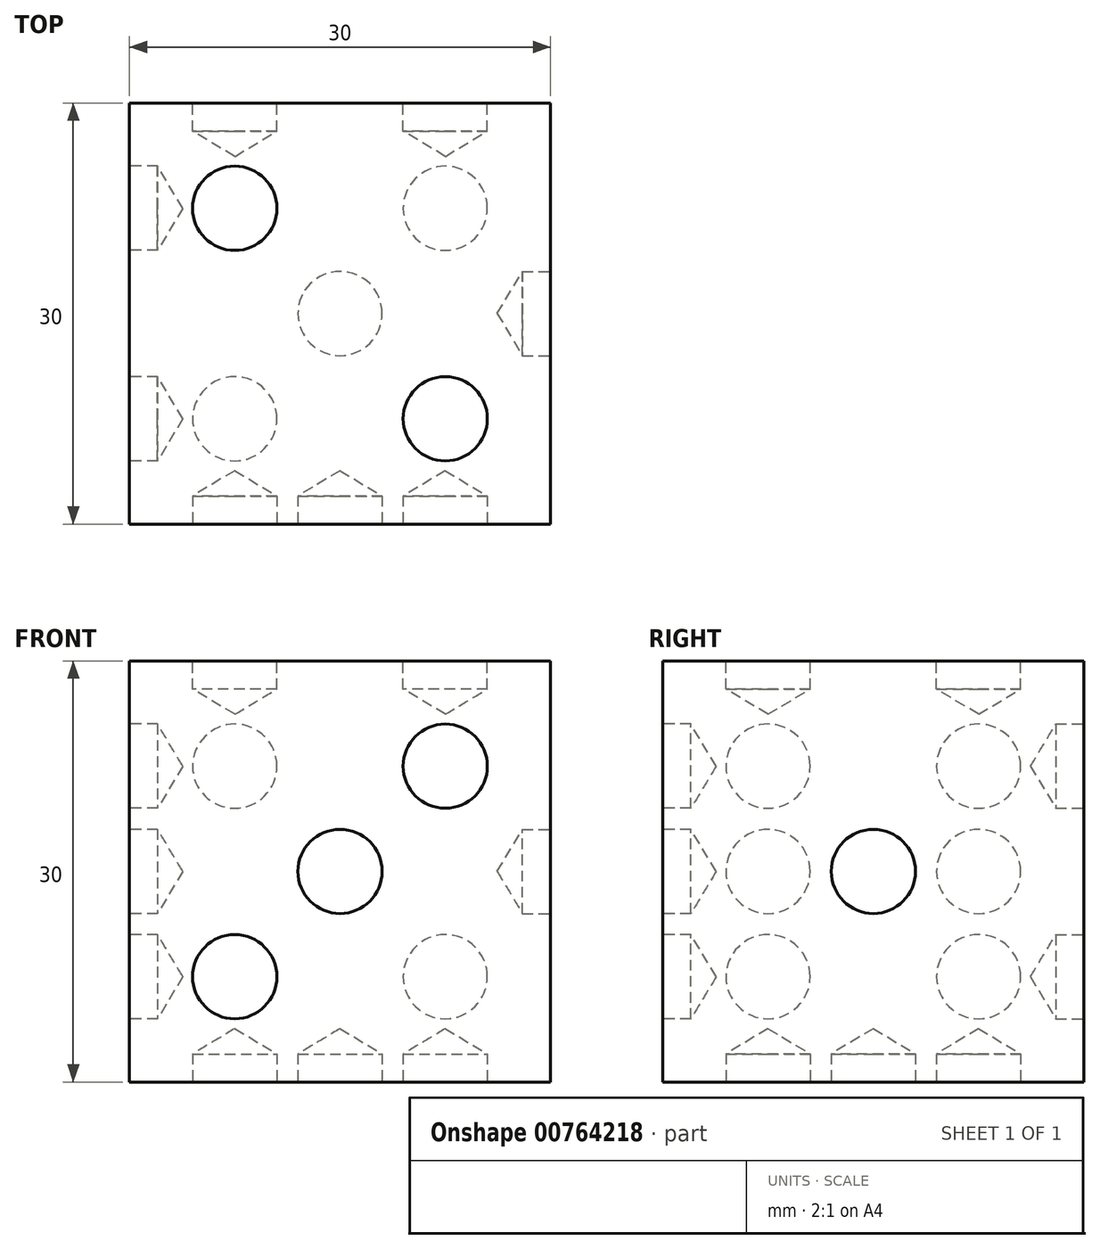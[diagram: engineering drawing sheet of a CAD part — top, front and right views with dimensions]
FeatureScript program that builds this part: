
annotation { "Feature Type Name" : "Feature", "Feature Type Description" : "" }
export const myFeature = defineFeature(function(context is Context, id is Id, definition is map)
    precondition{}
    {
        {
            var Q0;
            Q0=qCreatedBy(makeId("Front.planeOp"),FACE);
            var sketch = newSketch(context, id + "F0", { "sketchPlane" : qUnion([Q0])});
            skLineSegment(sketch, "E0.bottom", {"start": v(-15, 15) * mm, "end": v(15, 15) * mm});
            skLineSegment(sketch, "E0.top", {"start": v(-15, -15) * mm, "end": v(15, -15) * mm});
            skLineSegment(sketch, "E0.left", {"start": v(-15, 15) * mm, "end": v(-15, -15) * mm});
            skLineSegment(sketch, "E0.right", {"start": v(15, 15) * mm, "end": v(15, -15) * mm});
            skPoint(sketch, "E0.middle", {"position": v(0, 0) * mm});
            skSolve(sketch);
        }
        {
            var Q0;
            Q0=makeQuery(id+"F0.imprint","IMPRINT",FACE,{"disambiguationData":[TD([[makeQuery(id+"F0.imprint","IMPRINT",EDGE,{"derivedFrom":sQuery(id+"F0.wireOp",EDGE,"E0.bottom")}),-1.0]])]});
            extrude(context, id + "F1", {"entities" : qUnion([Q0]), "endBound" : BoundingType.SYMMETRIC, "depth" : 30 * mm, "offsetDistance" : 25 * mm});
        }
        {
            var Q0;
            Q0=makeQuery(id+"F1.opExtrude","CAP_FACE",FACE,{"disambiguationData":[OSD([sQuery(id+"F0.wireOp",EDGE,"E0.bottom"),sQuery(id+"F0.wireOp",EDGE,"E0.top"),sQuery(id+"F0.wireOp",EDGE,"E0.left"),sQuery(id+"F0.wireOp",EDGE,"E0.right")])],"isStart":false});
            var sketch = newSketch(context, id + "F2", { "sketchPlane" : qUnion([Q0])});
            skLineSegment(sketch, "E1", {"start": v(0, 15) * mm, "end": v(15, 0) * mm});
            skLineSegment(sketch, "E2", {"start": v(15, 0) * mm, "end": v(0, -15) * mm});
            skLineSegment(sketch, "E3", {"start": v(0, -15) * mm, "end": v(-15, 0) * mm});
            skLineSegment(sketch, "E4", {"start": v(-15, 0) * mm, "end": v(0, 15) * mm});
            skLineSegment(sketch, "E5", {"start": v(-15, 15) * mm, "end": v(15, -15) * mm});
            skLineSegment(sketch, "E6", {"start": v(15, 15) * mm, "end": v(-15, -15) * mm});
            skLineSegment(sketch, "E7", {"start": v(-7.5, -7.5) * mm, "end": v(7.5, -7.5) * mm});
            skLineSegment(sketch, "E8", {"start": v(7.5, -7.5) * mm, "end": v(7.5, 7.5) * mm});
            skLineSegment(sketch, "E9", {"start": v(7.5, 7.5) * mm, "end": v(-7.5, 7.5) * mm});
            skLineSegment(sketch, "E10", {"start": v(-7.5, 7.5) * mm, "end": v(-7.5, -7.5) * mm});
            skLineSegment(sketch, "E11", {"start": v(-7.5, 0) * mm, "end": v(7.5, 0) * mm});
            skLineSegment(sketch, "E12", {"start": v(0, 7.5) * mm, "end": v(0, -7.5) * mm});
            skPoint(sketch, "E13", {"position": v(0, 0) * mm});
            skSolve(sketch);
        }
        {
            var Q0;
            Q0=makeQuery(id+"F1.opExtrude","SWEPT_FACE",FACE,{"disambiguationData":[OSD([sQuery(id+"F0.wireOp",EDGE,"E0.right")])]});
            var sketch = newSketch(context, id + "F3", { "sketchPlane" : qUnion([Q0])});
            skLineSegment(sketch, "E14", {"start": v(0, 15) * mm, "end": v(15, 0) * mm});
            skLineSegment(sketch, "E15", {"start": v(15, 0) * mm, "end": v(0, -15) * mm});
            skLineSegment(sketch, "E16", {"start": v(0, -15) * mm, "end": v(-15, 0) * mm});
            skLineSegment(sketch, "E17", {"start": v(-15, 0) * mm, "end": v(0, 15) * mm});
            skLineSegment(sketch, "E18", {"start": v(-15, 15) * mm, "end": v(15, -15) * mm});
            skLineSegment(sketch, "E19", {"start": v(15, 15) * mm, "end": v(-15, -15) * mm});
            skLineSegment(sketch, "E20", {"start": v(-7.5, -7.5) * mm, "end": v(7.5, -7.5) * mm});
            skLineSegment(sketch, "E21", {"start": v(7.5, -7.5) * mm, "end": v(7.5, 7.5) * mm});
            skLineSegment(sketch, "E22", {"start": v(7.5, 7.5) * mm, "end": v(-7.5, 7.5) * mm});
            skLineSegment(sketch, "E23", {"start": v(-7.5, 7.5) * mm, "end": v(-7.5, -7.5) * mm});
            skLineSegment(sketch, "E24", {"start": v(-7.5, 0) * mm, "end": v(7.5, 0) * mm});
            skLineSegment(sketch, "E25", {"start": v(0, 7.5) * mm, "end": v(0, -7.5) * mm});
            skPoint(sketch, "E26", {"position": v(0, 0) * mm});
            skSolve(sketch);
        }
        {
            var Q0;
            Q0=makeQuery(id+"F1.opExtrude","SWEPT_FACE",FACE,{"disambiguationData":[OSD([sQuery(id+"F0.wireOp",EDGE,"E0.bottom")])]});
            var sketch = newSketch(context, id + "F4", { "sketchPlane" : qUnion([Q0])});
            skLineSegment(sketch, "E27", {"start": v(0, 15) * mm, "end": v(15, 0) * mm});
            skLineSegment(sketch, "E28", {"start": v(15, 0) * mm, "end": v(0, -15) * mm});
            skLineSegment(sketch, "E29", {"start": v(0, -15) * mm, "end": v(-15, 0) * mm});
            skLineSegment(sketch, "E30", {"start": v(-15, 0) * mm, "end": v(0, 15) * mm});
            skLineSegment(sketch, "E31", {"start": v(-15, 15) * mm, "end": v(15, -15) * mm});
            skLineSegment(sketch, "E32", {"start": v(15, 15) * mm, "end": v(-15, -15) * mm});
            skLineSegment(sketch, "E33", {"start": v(-7.5, -7.5) * mm, "end": v(7.5, -7.5) * mm});
            skLineSegment(sketch, "E34", {"start": v(7.5, -7.5) * mm, "end": v(7.5, 7.5) * mm});
            skLineSegment(sketch, "E35", {"start": v(7.5, 7.5) * mm, "end": v(-7.5, 7.5) * mm});
            skLineSegment(sketch, "E36", {"start": v(-7.5, 7.5) * mm, "end": v(-7.5, -7.5) * mm});
            skLineSegment(sketch, "E37", {"start": v(-7.5, 0) * mm, "end": v(7.5, 0) * mm});
            skLineSegment(sketch, "E38", {"start": v(0, 7.5) * mm, "end": v(0, -7.5) * mm});
            skPoint(sketch, "E39", {"position": v(0, 0) * mm});
            skSolve(sketch);
        }
        {
            var Q0;
            Q0=makeQuery(id+"F1.opExtrude","CAP_FACE",FACE,{"disambiguationData":[OSD([sQuery(id+"F0.wireOp",EDGE,"E0.bottom"),sQuery(id+"F0.wireOp",EDGE,"E0.top"),sQuery(id+"F0.wireOp",EDGE,"E0.left"),sQuery(id+"F0.wireOp",EDGE,"E0.right")])],"isStart":true});
            var sketch = newSketch(context, id + "F5", { "sketchPlane" : qUnion([Q0])});
            skLineSegment(sketch, "E40", {"start": v(0, 15) * mm, "end": v(15, 0) * mm});
            skLineSegment(sketch, "E41", {"start": v(15, 0) * mm, "end": v(0, -15) * mm});
            skLineSegment(sketch, "E42", {"start": v(0, -15) * mm, "end": v(-15, 0) * mm});
            skLineSegment(sketch, "E43", {"start": v(-15, 0) * mm, "end": v(0, 15) * mm});
            skLineSegment(sketch, "E44", {"start": v(-15, 15) * mm, "end": v(15, -15) * mm});
            skLineSegment(sketch, "E45", {"start": v(15, 15) * mm, "end": v(-15, -15) * mm});
            skLineSegment(sketch, "E46", {"start": v(-7.5, -7.5) * mm, "end": v(7.5, -7.5) * mm});
            skLineSegment(sketch, "E47", {"start": v(7.5, -7.5) * mm, "end": v(7.5, 7.5) * mm});
            skLineSegment(sketch, "E48", {"start": v(7.5, 7.5) * mm, "end": v(-7.5, 7.5) * mm});
            skLineSegment(sketch, "E49", {"start": v(-7.5, 7.5) * mm, "end": v(-7.5, -7.5) * mm});
            skLineSegment(sketch, "E50", {"start": v(-7.5, 0) * mm, "end": v(7.5, 0) * mm});
            skLineSegment(sketch, "E51", {"start": v(0, 7.5) * mm, "end": v(0, -7.5) * mm});
            skPoint(sketch, "E52", {"position": v(0, 0) * mm});
            skSolve(sketch);
        }
        {
            var Q0;
            Q0=makeQuery(id+"F1.opExtrude","SWEPT_FACE",FACE,{"disambiguationData":[OSD([sQuery(id+"F0.wireOp",EDGE,"E0.top")])]});
            var sketch = newSketch(context, id + "F6", { "sketchPlane" : qUnion([Q0])});
            skLineSegment(sketch, "E53", {"start": v(0, 15) * mm, "end": v(15, 0) * mm});
            skLineSegment(sketch, "E54", {"start": v(15, 0) * mm, "end": v(0, -15) * mm});
            skLineSegment(sketch, "E55", {"start": v(0, -15) * mm, "end": v(-15, 0) * mm});
            skLineSegment(sketch, "E56", {"start": v(-15, 0) * mm, "end": v(0, 15) * mm});
            skLineSegment(sketch, "E57", {"start": v(-15, 15) * mm, "end": v(15, -15) * mm});
            skLineSegment(sketch, "E58", {"start": v(15, 15) * mm, "end": v(-15, -15) * mm});
            skLineSegment(sketch, "E59", {"start": v(-7.5, -7.5) * mm, "end": v(7.5, -7.5) * mm});
            skLineSegment(sketch, "E60", {"start": v(7.5, -7.5) * mm, "end": v(7.5, 7.5) * mm});
            skLineSegment(sketch, "E61", {"start": v(7.5, 7.5) * mm, "end": v(-7.5, 7.5) * mm});
            skLineSegment(sketch, "E62", {"start": v(-7.5, 7.5) * mm, "end": v(-7.5, -7.5) * mm});
            skLineSegment(sketch, "E63", {"start": v(-7.5, 0) * mm, "end": v(7.5, 0) * mm});
            skLineSegment(sketch, "E64", {"start": v(0, 7.5) * mm, "end": v(0, -7.5) * mm});
            skPoint(sketch, "E65", {"position": v(0, 0) * mm});
            skSolve(sketch);
        }
        {
            var Q0;
            Q0=makeQuery(id+"F1.opExtrude","SWEPT_FACE",FACE,{"disambiguationData":[OSD([sQuery(id+"F0.wireOp",EDGE,"E0.left")])]});
            var sketch = newSketch(context, id + "F7", { "sketchPlane" : qUnion([Q0])});
            skLineSegment(sketch, "E66", {"start": v(0, 15) * mm, "end": v(15, 0) * mm});
            skLineSegment(sketch, "E67", {"start": v(15, 0) * mm, "end": v(0, -15) * mm});
            skLineSegment(sketch, "E68", {"start": v(0, -15) * mm, "end": v(-15, 0) * mm});
            skLineSegment(sketch, "E69", {"start": v(-15, 0) * mm, "end": v(0, 15) * mm});
            skLineSegment(sketch, "E70", {"start": v(-15, 15) * mm, "end": v(15, -15) * mm});
            skLineSegment(sketch, "E71", {"start": v(15, 15) * mm, "end": v(-15, -15) * mm});
            skLineSegment(sketch, "E72", {"start": v(-7.5, -7.5) * mm, "end": v(7.5, -7.5) * mm});
            skLineSegment(sketch, "E73", {"start": v(7.5, -7.5) * mm, "end": v(7.5, 7.5) * mm});
            skLineSegment(sketch, "E74", {"start": v(7.5, 7.5) * mm, "end": v(-7.5, 7.5) * mm});
            skLineSegment(sketch, "E75", {"start": v(-7.5, 7.5) * mm, "end": v(-7.5, -7.5) * mm});
            skLineSegment(sketch, "E76", {"start": v(-7.5, 0) * mm, "end": v(7.5, 0) * mm});
            skLineSegment(sketch, "E77", {"start": v(0, 7.5) * mm, "end": v(0, -7.5) * mm});
            skPoint(sketch, "E78", {"position": v(0, 0) * mm});
            skSolve(sketch);
        }
        {
            var Q0;
            Q0=sQuery(id+"F2.wireOp",VERTEX,"E9.start");
            var Q1;
            Q1=sQuery(id+"F2.wireOp",VERTEX,"E13");
            var Q2;
            Q2=sQuery(id+"F2.wireOp",VERTEX,"E10.end");
            var Q3;
            Q3=sQuery(id+"F5.wireOp",VERTEX,"E49.start");
            var Q4;
            Q4=sQuery(id+"F5.wireOp",VERTEX,"E47.end");
            var Q5;
            Q5=sQuery(id+"F5.wireOp",VERTEX,"E47.start");
            var Q6;
            Q6=sQuery(id+"F5.wireOp",VERTEX,"E49.end");
            var Q7;
            Q7=sQuery(id+"F7.wireOp",VERTEX,"E75.start");
            var Q8;
            Q8=sQuery(id+"F7.wireOp",VERTEX,"E76.start");
            var Q9;
            Q9=sQuery(id+"F7.wireOp",VERTEX,"E75.end");
            var Q10;
            Q10=sQuery(id+"F7.wireOp",VERTEX,"E73.start");
            var Q11;
            Q11=sQuery(id+"F7.wireOp",VERTEX,"E76.end");
            var Q12;
            Q12=sQuery(id+"F7.wireOp",VERTEX,"E74.start");
            var Q13;
            Q13=sQuery(id+"F3.wireOp",VERTEX,"E26");
            var Q14;
            Q14=sQuery(id+"F4.wireOp",VERTEX,"E36.start");
            var Q15;
            Q15=sQuery(id+"F4.wireOp",VERTEX,"E34.start");
            var Q16;
            Q16=sQuery(id+"F6.wireOp",VERTEX,"E62.end");
            var Q17;
            Q17=sQuery(id+"F6.wireOp",VERTEX,"E65");
            var Q18;
            Q18=sQuery(id+"F6.wireOp",VERTEX,"E60.end");
            var Q19;
            Q19=sQuery(id+"F6.wireOp",VERTEX,"E62.start");
            var Q20;
            Q20=sQuery(id+"F6.wireOp",VERTEX,"E60.start");
            var Q21;
            Q21=makeQuery(id+"F1.opExtrude","SWEPT_BODY",BODY,{"disambiguationData":[OSD([sQuery(id+"F0.wireOp",EDGE,"E0.bottom"),sQuery(id+"F0.wireOp",EDGE,"E0.top"),sQuery(id+"F0.wireOp",EDGE,"E0.left"),sQuery(id+"F0.wireOp",EDGE,"E0.right")])]});
            hole(context, id + "F8", {"style" : HoleStyle.C_BORE, "endStyle" : HoleEndStyle.BLIND, "holeDiameter" : 6 * mm, "cBoreDiameter" : 6 * mm, "cBoreDepth" : 2 * mm, "holeDepth" : 2 * mm, "locations" : qUnion([Q0, Q1, Q2, Q3, Q4, Q5, Q6, Q7, Q8, Q9, Q10, Q11, Q12, Q13, Q14, Q15, Q16, Q17, Q18, Q19, Q20]), "scope" : qUnion([Q21])});
        }
    });
